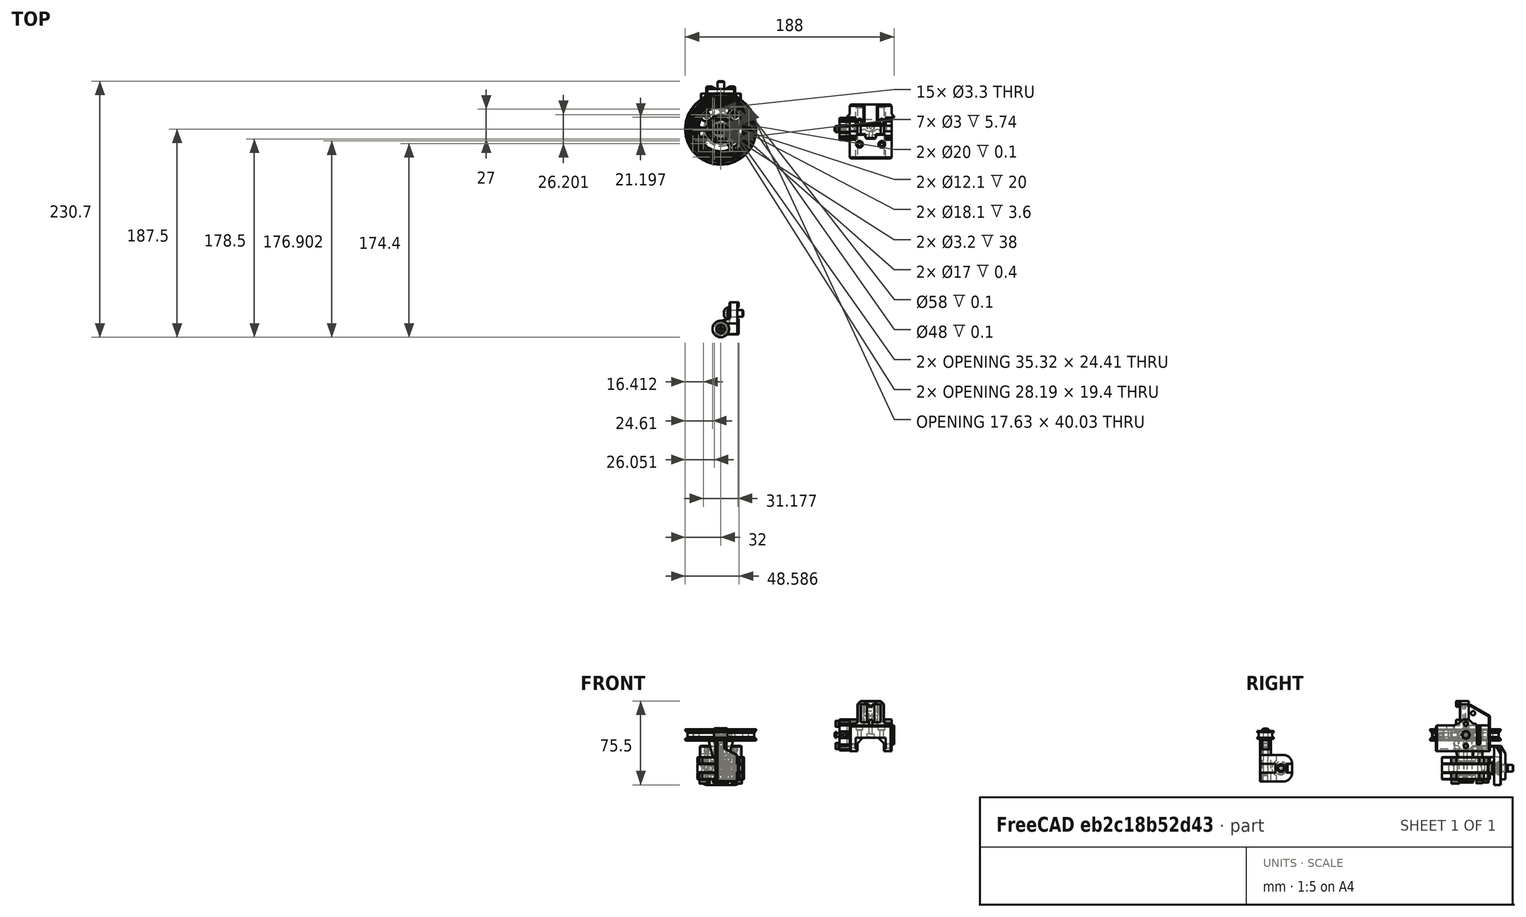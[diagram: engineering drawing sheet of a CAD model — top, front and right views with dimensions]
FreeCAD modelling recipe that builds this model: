
FCSTD DOCUMENT  (FreeCAD 0.19R24291 (Git))
Label: z-counter-weight-assembly
License: Other
LicenseURL: GPL3
objects: Part::FeaturePython×32, Part::Feature×15, App::Part×3
note: 47 computed .brp shape members not serialized (recipe doc carries the construction recipe); baked Part::Feature solids carry a one-line shape summary decoded from their .brp

FEATURE [Part::Feature] Chamfer001001001  label="bearing-6701ZZ1"
  shape: bbox 18 x 18 x 4 mm, 20 faces (baked)
FEATURE [Part::Feature] Chamfer002001001  label="bearing-6701ZZ2"
  shape: bbox 18 x 18 x 4 mm, 20 faces (baked)
FEATURE [Part::Feature] Chamfer005001001  label="housing-middle"
  shape: bbox 42 x 41.91 x 12.4 mm, 58 faces (baked)
FEATURE [Part::Feature] Chamfer006001001  label="housing-front"
  shape: bbox 42 x 43 x 6 mm, 58 faces (baked)
FEATURE [Part::Feature] Chamfer007001001  label="housing-back"
  shape: bbox 42 x 43 x 6 mm, 55 faces (baked)
FEATURE [Part::Feature] Body001001001002001001001  label="pylley-25mm"
  shape: bbox 54 x 54 x 25 mm, 117 faces (baked)
FEATURE [Part::Feature] Body001001001002002001001  label="pulley-30mm"
  shape: bbox 64 x 64 x 25 mm, 117 faces (baked)
FEATURE [Part::Feature] Chamfer026009001001  label="250-mounter"
  shape: bbox 37.46 x 26.27 x 35 mm, 48 faces (baked)
FEATURE [Part::Feature] Fusion001002009001001  label="180-mounter"
  shape: bbox 37.46 x 30.27 x 30 mm, 47 faces (baked)
FEATURE [Part::Feature] Body001001001002003005001001  label="U624ZZ-bearing"
  Placement = pos=(0,-120,0) rot=(0,0,1;0rad)
  shape: bbox 15 x 15 x 7 mm, 6 faces (baked)
FEATURE [Part::Feature] Body001001001002003006001001  label="top-bearing-arm"
  Placement = pos=(5,-120,25) rot=(0,0,1;0rad)
  shape: bbox 21 x 29 x 37.5 mm, 62 faces (baked)
FEATURE [Part::Feature] Body001001001002003007001001  label="spacer"
  Placement = pos=(0,-180,35.5) rot=(0,0,1;0rad)
  shape: bbox 7 x 7 x 1 mm, 4 faces (baked)
FEATURE [Part::Feature] Body003001  label="axis"
  Placement = pos=(0,0,-3) rot=(0,0,1;0rad)
  shape: bbox 14.1 x 14.1 x 43 mm, 25 faces (baked)
FEATURE [Part::FeaturePython] Screw  label="M3x20-Screw"  # Fasteners workbench fastener (typed FeaturePython)
  Placement = pos=(0,18,0) rot=(-1,0,0;3.14159rad)
  baseObject = -> Chamfer007001001 [Edge120]
  diameter = 4
  invert = true
  length = 7
  lengthCustom = 20
  matchOuter = true
  offset = 0
  thread = false
  type = 34
FEATURE [Part::FeaturePython] Screw001  label="M4x20-Screw001"  # Fasteners workbench fastener (typed FeaturePython)
  Placement = pos=(15.5885,-9,0) rot=(-1,0,0;3.14159rad)
  baseObject = -> Chamfer007001001 [Edge116]
  diameter = 5
  invert = true
  length = 6
  lengthCustom = 20
  matchOuter = true
  offset = 0
  thread = false
  type = 34
FEATURE [Part::FeaturePython] Screw002  label="M4x20-Screw002"  # Fasteners workbench fastener (typed FeaturePython)
  Placement = pos=(-15.5885,-9,0) rot=(-1,0,0;3.14159rad)
  baseObject = -> Chamfer007001001 [Edge118]
  diameter = 5
  invert = true
  length = 6
  lengthCustom = 20
  matchOuter = true
  offset = 0
  thread = false
  type = 34
FEATURE [Part::FeaturePython] Washer  label="M3-Washer"  # Fasteners workbench fastener (typed FeaturePython)
  Placement = pos=(-12.7279,12.7279,0) rot=(-1,0,0;3.14159rad)
  baseObject = -> Chamfer007001001 [Edge114]
  diameter = 4
  invert = true
  matchOuter = true
  offset = 0
  type = 5
FEATURE [Part::FeaturePython] Washer001  label="M3-Washer001"  # Fasteners workbench fastener (typed FeaturePython)
  Placement = pos=(12.7279,12.7279,0) rot=(-1,0,0;3.14159rad)
  baseObject = -> Chamfer007001001 [Edge112]
  diameter = 4
  invert = true
  matchOuter = true
  offset = 0
  type = 5
FEATURE [Part::FeaturePython] Screw003  label="M3x30-Screw"  # Fasteners workbench fastener (typed FeaturePython)
  Placement = pos=(-12.7279,12.7279,-0.55) rot=(-1,0,0;3.14159rad)
  baseObject = -> Washer [Edge1]
  diameter = 4
  invert = false
  length = 9
  lengthCustom = 30
  matchOuter = true
  offset = 0
  thread = false
  type = 34
FEATURE [Part::FeaturePython] Screw004  label="M3x30-Screw001"  # Fasteners workbench fastener (typed FeaturePython)
  Placement = pos=(12.7279,12.7279,-0.55) rot=(-1,0,0;3.14159rad)
  baseObject = -> Washer001 [Edge1]
  diameter = 4
  invert = false
  length = 9
  lengthCustom = 30
  matchOuter = true
  offset = 0
  thread = false
  type = 34
FEATURE [Part::FeaturePython] HeatSet  label="M3-HeatSet"  # WARN: FeaturePython — macro-defined, semantics opaque (R4)
  Placement = pos=(12.7279,12.7279,30) rot=(0,0,1;0rad)
  baseObject = -> Chamfer026009001001 [Edge8]
  diameter = 2
  invert = false
  offset = 0
FEATURE [Part::FeaturePython] HeatSet001  label="M3-HeatSet001"  # WARN: FeaturePython — macro-defined, semantics opaque (R4)
  Placement = pos=(-12.7279,12.7279,30) rot=(0,0,1;0rad)
  baseObject = -> Chamfer026009001001 [Edge2]
  diameter = 2
  invert = false
  offset = 0
FEATURE [Part::FeaturePython] HeatSet002  label="M3-HeatSet002"  # WARN: FeaturePython — macro-defined, semantics opaque (R4)
  Placement = pos=(15.5885,-9,20) rot=(0,0,1;0rad)
  baseObject = -> Chamfer006001001 [Edge45]
  diameter = 2
  invert = false
  offset = 0
FEATURE [Part::FeaturePython] HeatSet003  label="M3-HeatSet003"  # WARN: FeaturePython — macro-defined, semantics opaque (R4)
  Placement = pos=(0,18,20) rot=(0,0,1;0rad)
  baseObject = -> Chamfer006001001 [Edge44]
  diameter = 2
  invert = false
  offset = 0
FEATURE [Part::FeaturePython] HeatSet004  label="M3-HeatSet004"  # WARN: FeaturePython — macro-defined, semantics opaque (R4)
  Placement = pos=(-15.5885,-9,20) rot=(0,0,1;0rad)
  baseObject = -> Chamfer006001001 [Edge46]
  diameter = 2
  invert = false
  offset = 0
FEATURE [Part::FeaturePython] HeatSet005  label="M3-HeatSet005"  # WARN: FeaturePython — macro-defined, semantics opaque (R4)
  Placement = pos=(-3,0,-3) rot=(-1,0,0;3.14159rad)
  baseObject = -> Body003001 [Edge7]
  diameter = 2
  invert = true
  offset = 0
FEATURE [Part::FeaturePython] HeatSet006  label="M3-HeatSet006"  # WARN: FeaturePython — macro-defined, semantics opaque (R4)
  Placement = pos=(3,0,-3) rot=(-1,0,0;3.14159rad)
  baseObject = -> Body003001 [Edge8]
  diameter = 2
  invert = true
  offset = 0
FEATURE [Part::FeaturePython] Screw005  label="M3x45-Screw"  # Fasteners workbench fastener (typed FeaturePython)
  Placement = pos=(3,-2.6e-14,43) rot=(0,0,1;0rad)
  baseObject = -> Body001001001002001001001 [Edge239]
  diameter = 4
  invert = false
  length = 10
  lengthCustom = 45
  matchOuter = true
  offset = 0
  thread = false
  type = 34
FEATURE [Part::FeaturePython] Screw006  label="M3x45-Screw001"  # Fasteners workbench fastener (typed FeaturePython)
  Placement = pos=(-3,-2.4e-14,43) rot=(0,0,1;0rad)
  baseObject = -> Body001001001002001001001 [Edge237]
  diameter = 4
  invert = false
  length = 10
  lengthCustom = 45
  matchOuter = true
  offset = 0
  thread = false
  type = 34
FEATURE [Part::FeaturePython] Washer002  label="M6-Washer"  # Fasteners workbench fastener (typed FeaturePython)
  Placement = pos=(-10,26,10) rot=(1,0,0;1.5708rad)
  baseObject = -> Chamfer026009001001 [Edge17]
  diameter = 2
  invert = false
  matchOuter = true
  offset = 0
  type = 4
FEATURE [Part::FeaturePython] Washer003  label="M6-Washer001"  # Fasteners workbench fastener (typed FeaturePython)
  Placement = pos=(10,26,10) rot=(1,0,0;1.5708rad)
  baseObject = -> Chamfer026009001001 [Edge23]
  diameter = 2
  invert = false
  matchOuter = true
  offset = 0
  type = 4
FEATURE [Part::FeaturePython] Screw007  label="M6x14-Screw003"  # Fasteners workbench fastener (typed FeaturePython)
  Placement = pos=(10,24.2,10) rot=(1,0,0;1.5708rad)
  baseObject = -> Washer003 [Edge1]
  diameter = 4
  invert = false
  length = 2
  lengthCustom = 14
  matchOuter = true
  offset = 0
  thread = false
  type = 40
FEATURE [Part::FeaturePython] Screw008  label="M6x14-Screw004"  # Fasteners workbench fastener (typed FeaturePython)
  Placement = pos=(-10,24.2,10) rot=(1,0,0;1.5708rad)
  baseObject = -> Washer002 [Edge1]
  diameter = 4
  invert = false
  length = 2
  lengthCustom = 14
  matchOuter = true
  offset = 0
  thread = false
  type = 40
FEATURE [Part::FeaturePython] Washer004  label="M6-Washer002"  # Fasteners workbench fastener (typed FeaturePython)
  Placement = pos=(0,31,10) rot=(1,0,0;1.5708rad)
  baseObject = -> Fusion001002009001001 [Edge26]
  diameter = 2
  invert = false
  matchOuter = true
  offset = 0
  type = 4
FEATURE [Part::FeaturePython] Screw009  label="M6x14-Screw"  # Fasteners workbench fastener (typed FeaturePython)
  Placement = pos=(0,29.2,10) rot=(1,0,0;1.5708rad)
  baseObject = -> Washer004 [Edge1]
  diameter = 4
  invert = false
  length = 2
  lengthCustom = 14
  matchOuter = true
  offset = 0
  thread = false
  type = 40
FEATURE [App::Part] Part  label="spring-box"
  Group = -> [Chamfer001001001,Chamfer002001001,Chamfer005001001,Chamfer006001001,Chamfer007001001,Body001001001002001001001,Body001001001002002001001,Chamfer026009001001,Fusion001002009001001,Body003001,Screw009,Washer004,Screw,Screw001,Screw002,Washer,Washer001,Screw003,Screw004,HeatSet,HeatSet001,HeatSet002,HeatSet003,HeatSet004,HeatSet005,HeatSet006,Screw005,Screw006,Washer002,Washer003,Screw007,Screw008]
  Origin = -> Origin
FEATURE [Part::FeaturePython] Washer005  label="M6-Washer003"  # Fasteners workbench fastener (typed FeaturePython)
  Placement = pos=(8,-166,10) rot=(0,-1,0;1.5708rad)
  baseObject = -> Body001001001002003006001001 [Edge143]
  diameter = 2
  invert = true
  matchOuter = true
  offset = 0
  type = 4
FEATURE [Part::FeaturePython] Screw010  label="M6x14-Screw005"  # Fasteners workbench fastener (typed FeaturePython)
  Placement = pos=(6.2,-166,10) rot=(0,-1,0;1.5708rad)
  baseObject = -> Washer005 [Edge1]
  diameter = 4
  invert = false
  length = 2
  lengthCustom = 14
  matchOuter = true
  offset = 0
  thread = false
  type = 40
FEATURE [Part::FeaturePython] Screw011  label="M4x40-Screw"  # Fasteners workbench fastener (typed FeaturePython)
  Placement = pos=(-9e-15,-180,43.5) rot=(0,0,1;0rad)
  baseObject = -> Body001001001002003005001001 [Edge9]
  diameter = 2
  invert = true
  length = 10
  lengthCustom = 40
  matchOuter = true
  offset = 0
  thread = false
  type = 40
FEATURE [Part::FeaturePython] HeatSet007  label="M4-HeatSet"  # WARN: FeaturePython — macro-defined, semantics opaque (R4)
  Placement = pos=(0,-180,35.5) rot=(0,0,1;0rad)
  baseObject = -> Body001001001002003006001001 [Edge33]
  diameter = 4
  invert = false
  offset = 0
FEATURE [App::Part] Part001  label="top-pulley"
  Group = -> [Body001001001002003005001001,Body001001001002003006001001,Body001001001002003007001001,Washer005,Screw010,Screw011,HeatSet007]
  Origin = -> Origin001
  Placement = pos=(0,70,0) rot=(0,0,1;0rad)
FEATURE [Part::Feature] Chamfer026018001001  label="wire-mounter"
  Placement = pos=(116,0,40) rot=(0,1,0;4.71239rad)
  shape: bbox 9 x 20 x 28 mm, 41 faces (baked)
FEATURE [Part::FeaturePython] Washer006  label="M3-Washer004"  # Fasteners workbench fastener (typed FeaturePython)
  Placement = pos=(107,1.18e-14,50) rot=(0,-1,0;1.5708rad)
  baseObject = -> Chamfer026018001001 [Edge100]
  diameter = 4
  invert = true
  matchOuter = true
  offset = 0
  type = 5
FEATURE [Part::FeaturePython] Washer007  label="M3-Washer005"  # Fasteners workbench fastener (typed FeaturePython)
  Placement = pos=(107,1.18e-14,30) rot=(0,-1,0;1.5708rad)
  baseObject = -> Chamfer026018001001 [Edge101]
  diameter = 4
  invert = true
  matchOuter = true
  offset = 0
  type = 5
FEATURE [Part::FeaturePython] Screw012  label="M3x14-Screw"  # Fasteners workbench fastener (typed FeaturePython)
  Placement = pos=(106.45,1.19e-14,50) rot=(0,-1,0;1.5708rad)
  baseObject = -> Washer006 [Edge1]
  diameter = 4
  invert = false
  length = 5
  lengthCustom = 14
  matchOuter = true
  offset = 0
  thread = false
  type = 34
FEATURE [Part::FeaturePython] Screw013  label="M3x14-Screw001"  # Fasteners workbench fastener (typed FeaturePython)
  Placement = pos=(106.45,1.19e-14,30) rot=(0,-1,0;1.5708rad)
  baseObject = -> Washer007 [Edge1]
  diameter = 4
  invert = false
  length = 5
  lengthCustom = 14
  matchOuter = true
  offset = 0
  thread = false
  type = 34
FEATURE [Part::FeaturePython] HeatSet008  label="M3-HeatSet007"  # WARN: FeaturePython — macro-defined, semantics opaque (R4)
  Placement = pos=(107,0,40) rot=(0,-1,0;1.5708rad)
  baseObject = -> Chamfer026018001001 [Edge99]
  diameter = 2
  invert = false
  offset = 0
FEATURE [Part::FeaturePython] Screw014  label="M3x6-Screw"  # Fasteners workbench fastener (typed FeaturePython)
  Placement = pos=(104,0,40) rot=(0,-1,0;1.5708rad)
  baseObject = -> HeatSet008 [Edge1]
  diameter = 1
  invert = false
  length = 0
  lengthCustom = 6
  matchOuter = true
  offset = 3
  thread = false
  type = 40
FEATURE [Part::Feature] Fusion004025023015006011002001001  label="z-rail-block-mount-right-with-limiter-dual"
  Placement = pos=(135,19,37.5) rot=(0.57735,-0.57735,0.57735;2.0944rad)
  shape: bbox 42 x 48.4 x 45 mm, 134 faces (baked)
FEATURE [App::Part] Part002  label="z-rail-mount"
  Group = -> [Chamfer026018001001,Washer006,Washer007,Screw012,Screw013,HeatSet008,Screw014,Fusion004025023015006011002001001]
  Origin = -> Origin002
  Placement = pos=(-45,0,0) rot=(0,0,1;0rad)
